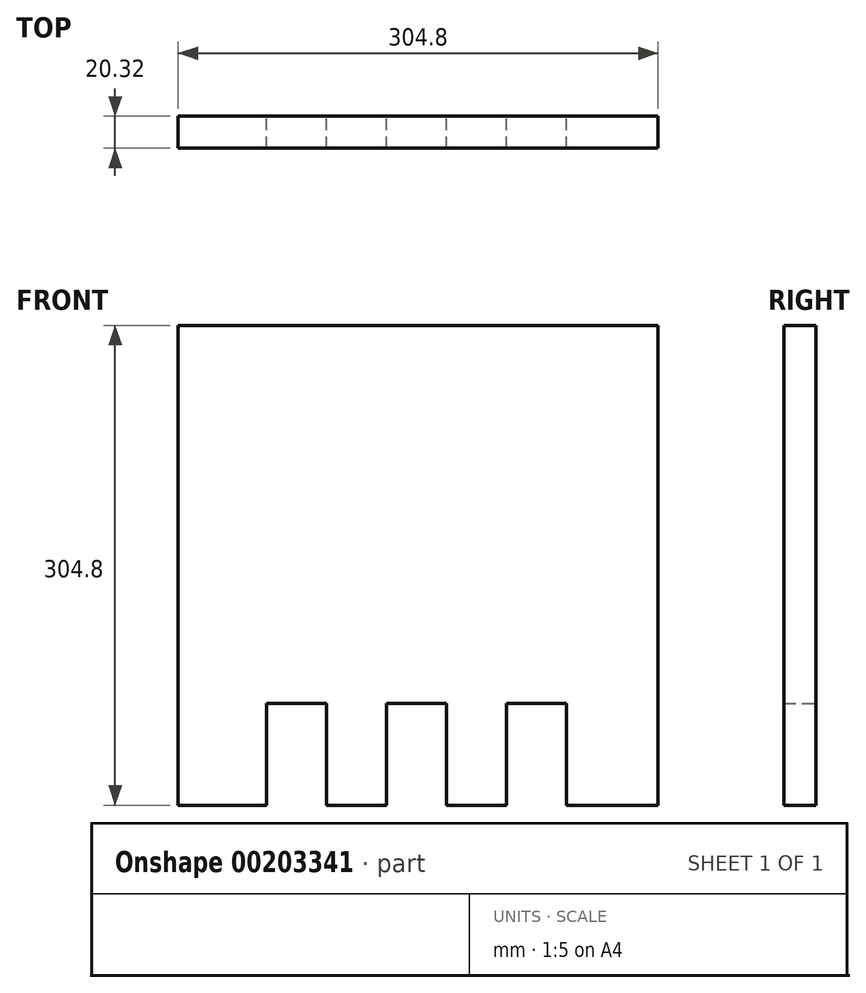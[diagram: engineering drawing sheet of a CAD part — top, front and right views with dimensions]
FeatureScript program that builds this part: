
annotation { "Feature Type Name" : "Feature", "Feature Type Description" : "" }
export const myFeature = defineFeature(function(context is Context, id is Id, definition is map)
    precondition{}
    {
        {
            var Q0;
            Q0=qCreatedBy(makeId("Front.planeOp"),FACE);
            var sketch = newSketch(context, id + "F0", { "sketchPlane" : qUnion([Q0])});
            skLineSegment(sketch, "E0", {"start": v(-146.11, 147.8) * mm, "end": v(158.69, 147.8) * mm});
            skLineSegment(sketch, "E1", {"start": v(158.69, 147.8) * mm, "end": v(158.69, -157) * mm});
            skLineSegment(sketch, "E2", {"start": v(-146.11, -157) * mm, "end": v(-146.11, 147.8) * mm});
            skLineSegment(sketch, "E3", {"start": v(-146.11, -157) * mm, "end": v(-90.02, -157) * mm});
            skLineSegment(sketch, "E4", {"start": v(-90.02, -157) * mm, "end": v(-90.02, -92.34) * mm});
            skLineSegment(sketch, "E5", {"start": v(-90.02, -92.34) * mm, "end": v(-51.92, -92.34) * mm});
            skLineSegment(sketch, "E6", {"start": v(-51.92, -92.34) * mm, "end": v(-51.92, -157) * mm});
            skLineSegment(sketch, "E7", {"start": v(-51.92, -157) * mm, "end": v(-13.82, -157) * mm});
            skLineSegment(sketch, "E8", {"start": v(-13.82, -157) * mm, "end": v(-13.82, -92.34) * mm});
            skLineSegment(sketch, "E9", {"start": v(-13.82, -92.34) * mm, "end": v(24.28, -92.34) * mm});
            skLineSegment(sketch, "E10", {"start": v(24.28, -92.34) * mm, "end": v(24.28, -157) * mm});
            skLineSegment(sketch, "E11", {"start": v(24.28, -157) * mm, "end": v(62.38, -157) * mm});
            skLineSegment(sketch, "E12", {"start": v(62.38, -157) * mm, "end": v(62.38, -92.34) * mm});
            skLineSegment(sketch, "E13", {"start": v(62.38, -92.34) * mm, "end": v(100.48, -92.34) * mm});
            skLineSegment(sketch, "E14", {"start": v(100.48, -92.34) * mm, "end": v(100.48, -157) * mm});
            skLineSegment(sketch, "E15", {"start": v(100.48, -157) * mm, "end": v(158.69, -157) * mm});
            skSolve(sketch);
        }
        {
            var Q0;
            Q0=makeQuery(id+"F0.imprint","IMPRINT",FACE,{"disambiguationData":[TD([[makeQuery(id+"F0.imprint","IMPRINT",EDGE,{"derivedFrom":sQuery(id+"F0.wireOp",EDGE,"E0")}),-1.0]])]});
            extrude(context, id + "F1", {"entities" : qUnion([Q0]), "endBound" : BoundingType.SYMMETRIC, "depth" : 20.32 * mm});
        }
    });
